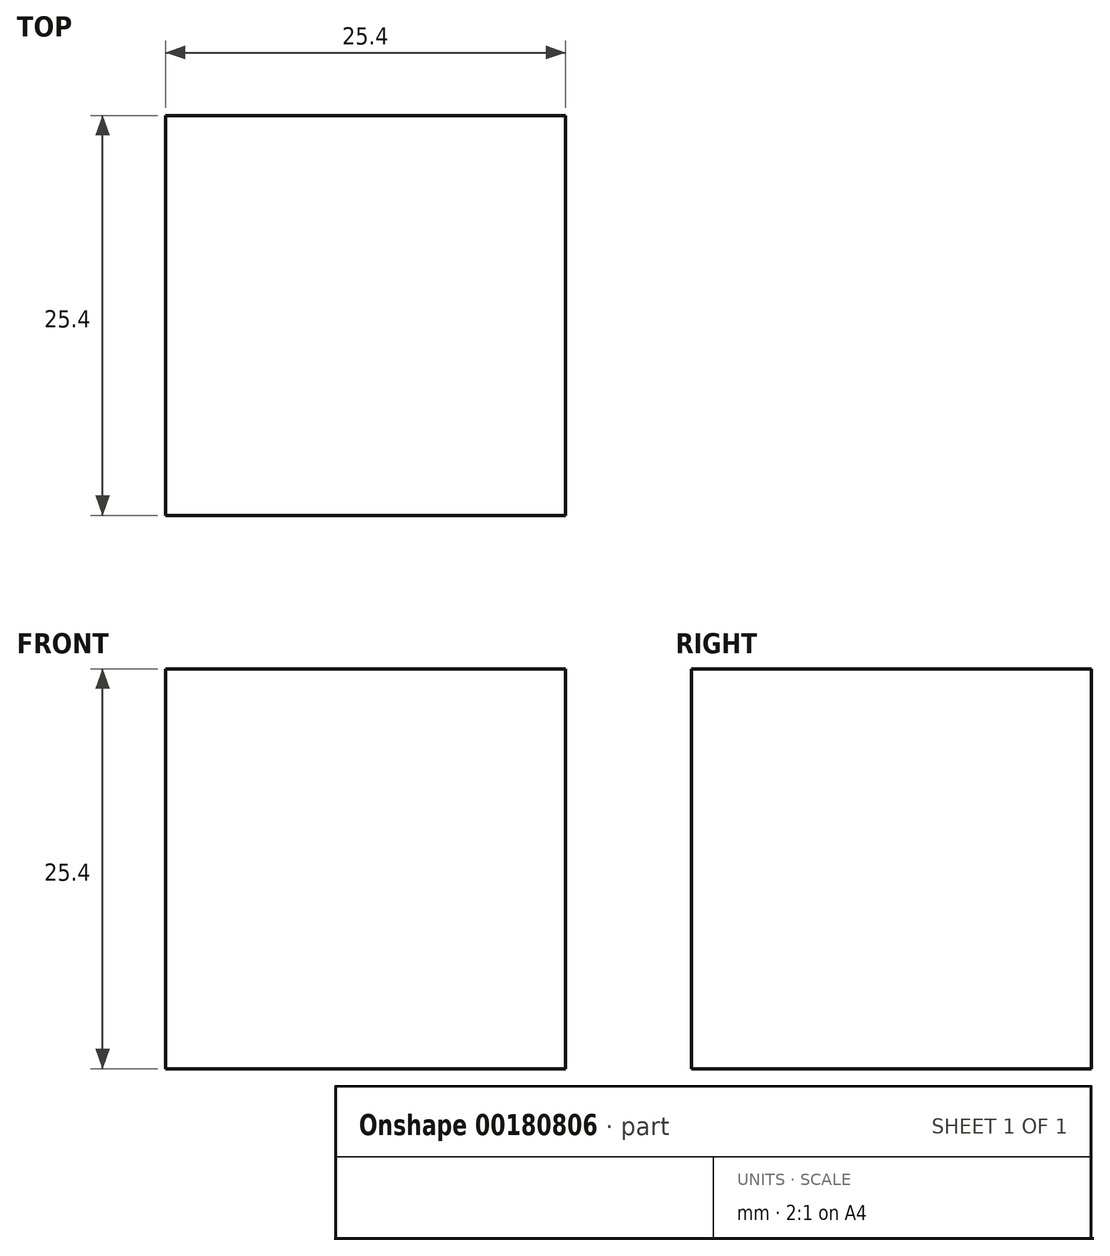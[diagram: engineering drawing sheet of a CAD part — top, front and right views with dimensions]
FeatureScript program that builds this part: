
annotation { "Feature Type Name" : "Feature", "Feature Type Description" : "" }
export const myFeature = defineFeature(function(context is Context, id is Id, definition is map)
    precondition{}
    {
        {
            var Q0;
            Q0=qCreatedBy(makeId("Top.planeOp"),FACE);
            var sketch = newSketch(context, id + "F0", { "sketchPlane" : qUnion([Q0])});
            skLineSegment(sketch, "E0", {"start": v(-12.7, 12.7) * mm, "end": v(-12.7, -12.7) * mm});
            skLineSegment(sketch, "E1.0", {"start": v(12.7, 12.7) * mm, "end": v(12.7, -12.7) * mm});
            skLineSegment(sketch, "E2", {"start": v(-12.7, 12.7) * mm, "end": v(12.7, 12.7) * mm});
            skLineSegment(sketch, "E3", {"start": v(-12.7, -12.7) * mm, "end": v(12.7, -12.7) * mm});
            skSolve(sketch);
        }
        {
            var Q0;
            Q0 = qSketchRegion(id + "F0", true);
            extrude(context, id + "F1", {"entities" : qUnion([Q0]), "depth" : 25.4 * mm});
        }
    });
